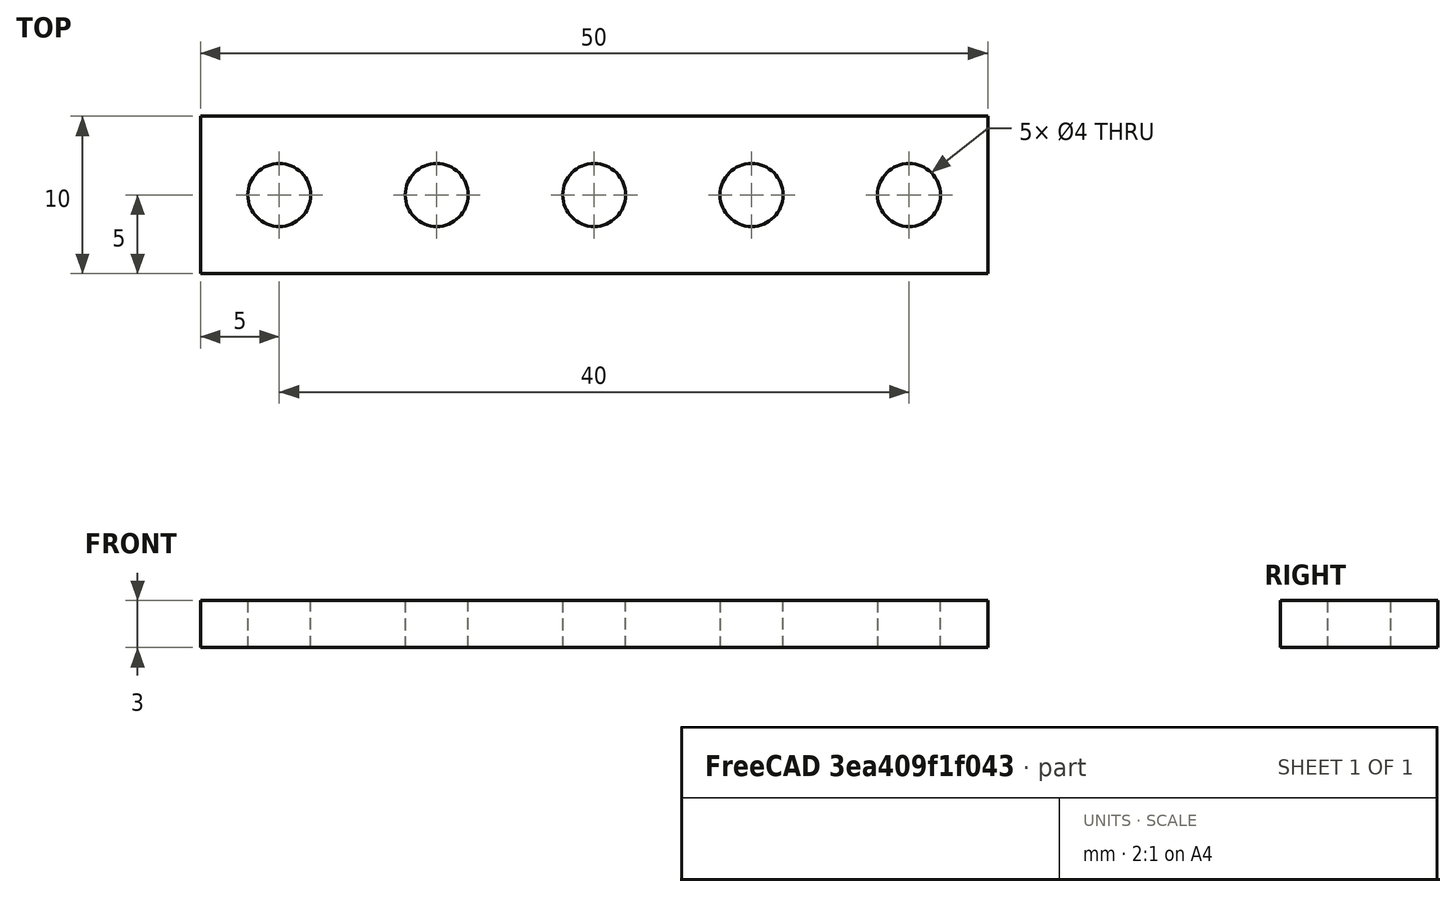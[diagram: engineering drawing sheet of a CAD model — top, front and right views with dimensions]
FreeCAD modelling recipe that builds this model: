
FCSTD DOCUMENT  (FreeCAD 0.20R29410 (Git))
Label: mecano
License: Creative Commons Attribution
LicenseURL: http://creativecommons.org/licenses/by/4.0/
objects: Part::Box×5, Part::Cylinder×5, Part::Cut×5, Part::Fuse×4
note: 19 computed .brp shape members not serialized (recipe doc carries the construction recipe); baked Part::Feature solids carry a one-line shape summary decoded from their .brp

FEATURE [Part::Box] Box  label="Cubo"
  AttacherType = Attacher::AttachEngine3D
  Height = 3
  Length = 10
  Width = 10
FEATURE [Part::Cylinder] Cylinder  label="Cilindro"
  Angle = 360
  AttacherType = Attacher::AttachEngine3D
  FirstAngle = 0
  Height = 10
  Placement = pos=(5,5,-2) rot=(0,0,1;0rad)
  Radius = 2
  SecondAngle = 0
FEATURE [Part::Cut] Cut
  Base = -> Box
  Refine = true
  Tool = -> Cylinder
FEATURE [Part::Box] Box001  label="Cubo001"
  AttacherType = Attacher::AttachEngine3D
  Height = 3
  Length = 10
  Width = 10
FEATURE [Part::Cylinder] Cylinder001  label="Cilindro001"
  Angle = 360
  AttacherType = Attacher::AttachEngine3D
  FirstAngle = 0
  Height = 10
  Placement = pos=(5,5,-2) rot=(0,0,1;0rad)
  Radius = 2
  SecondAngle = 0
FEATURE [Part::Cut] Cut001
  Base = -> Box001
  Placement = pos=(10,0,0) rot=(0,0,1;0rad)
  Refine = true
  Tool = -> Cylinder001
FEATURE [Part::Box] Box002  label="Cubo002"
  AttacherType = Attacher::AttachEngine3D
  Height = 3
  Length = 10
  Width = 10
FEATURE [Part::Cylinder] Cylinder002  label="Cilindro002"
  Angle = 360
  AttacherType = Attacher::AttachEngine3D
  FirstAngle = 0
  Height = 10
  Placement = pos=(5,5,-2) rot=(0,0,1;0rad)
  Radius = 2
  SecondAngle = 0
FEATURE [Part::Cut] Cut002
  Base = -> Box002
  Placement = pos=(20,0,0) rot=(0,0,1;0rad)
  Refine = true
  Tool = -> Cylinder002
FEATURE [Part::Box] Box003  label="Cubo003"
  AttacherType = Attacher::AttachEngine3D
  Height = 3
  Length = 10
  Width = 10
FEATURE [Part::Cylinder] Cylinder003  label="Cilindro003"
  Angle = 360
  AttacherType = Attacher::AttachEngine3D
  FirstAngle = 0
  Height = 10
  Placement = pos=(5,5,-2) rot=(0,0,1;0rad)
  Radius = 2
  SecondAngle = 0
FEATURE [Part::Cut] Cut003
  Base = -> Box003
  Placement = pos=(30,0,0) rot=(0,0,1;0rad)
  Refine = true
  Tool = -> Cylinder003
FEATURE [Part::Box] Box004  label="Cubo004"
  AttacherType = Attacher::AttachEngine3D
  Height = 3
  Length = 10
  Width = 10
FEATURE [Part::Cylinder] Cylinder004  label="Cilindro004"
  Angle = 360
  AttacherType = Attacher::AttachEngine3D
  FirstAngle = 0
  Height = 10
  Placement = pos=(5,5,-2) rot=(0,0,1;0rad)
  Radius = 2
  SecondAngle = 0
FEATURE [Part::Cut] Cut004
  Base = -> Box004
  Placement = pos=(40,0,0) rot=(0,0,1;0rad)
  Refine = true
  Tool = -> Cylinder004
FEATURE [Part::Fuse] Fusion
  Base = -> Cut
  Refine = true
  Tool = -> Cut001
FEATURE [Part::Fuse] Fusion001
  Base = -> Cut002
  Refine = true
  Tool = -> Fusion
FEATURE [Part::Fuse] Fusion002
  Base = -> Cut003
  Refine = true
  Tool = -> Fusion001
FEATURE [Part::Fuse] Fusion003
  Base = -> Cut004
  Refine = true
  Tool = -> Fusion002
